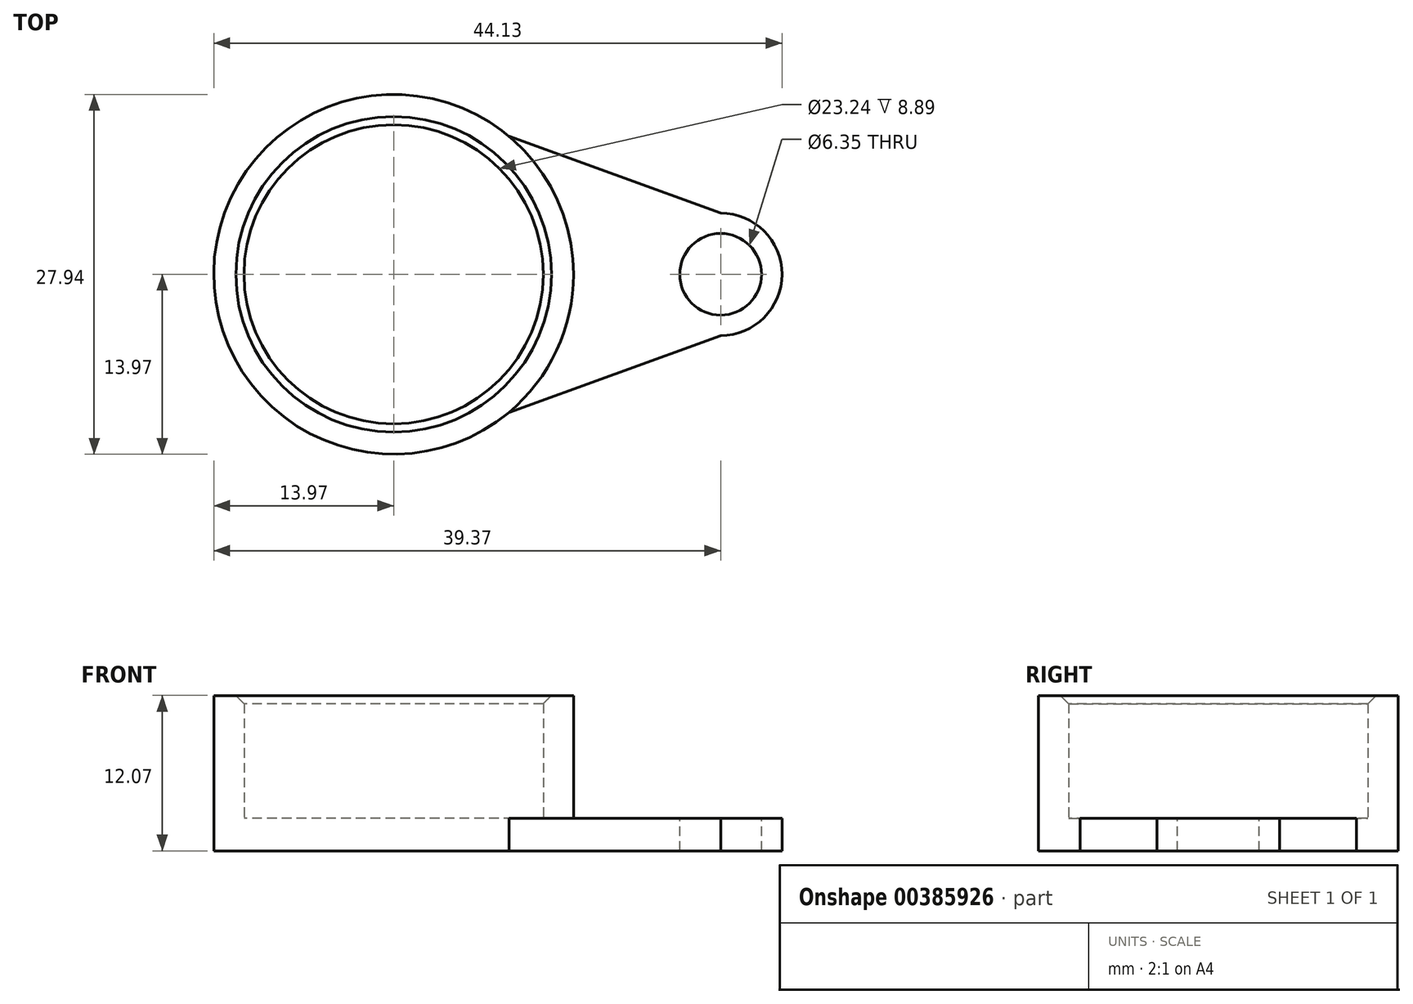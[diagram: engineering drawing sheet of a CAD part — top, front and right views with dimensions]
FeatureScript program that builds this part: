
annotation { "Feature Type Name" : "Feature", "Feature Type Description" : "" }
export const myFeature = defineFeature(function(context is Context, id is Id, definition is map)
    precondition{}
    {
        {
            var Q0;
            Q0=qCreatedBy(makeId("Top.planeOp"),FACE);
            var sketch = newSketch(context, id + "F0", { "sketchPlane" : qUnion([Q0])});
            skArc(sketch, "E0", {"start": v(8.95, 10.72) * mm, "mid": v(-13.97, 0) * mm, "end": v(8.95, -10.72) * mm});
            skArc(sketch, "E1", {"start": v(25.4, -4.76) * mm, "mid": v(30.16, 0) * mm, "end": v(25.4, 4.76) * mm});
            skLineSegment(sketch, "E2", {"start": v(8.95, -10.72) * mm, "end": v(25.4, -4.76) * mm});
            skPoint(sketch, "E3.orphan", {"position": v(25.4, 4.76) * mm});
            skPoint(sketch, "E4.start.orphan", {"position": v(0, 13.97) * mm});
            skLineSegment(sketch, "E5", {"start": v(8.95, 10.72) * mm, "end": v(25.4, 4.76) * mm});
            skPoint(sketch, "E6.orphan", {"position": v(0, -13.97) * mm});
            skSolve(sketch);
        }
        {
            var Q0;
            Q0=makeQuery(id+"F0.imprint","IMPRINT",FACE,{"disambiguationData":[TD([[makeQuery(id+"F0.imprint","IMPRINT",EDGE,{"derivedFrom":sQuery(id+"F0.wireOp",EDGE,"E0")}),1.0]])]});
            extrude(context, id + "F1", {"entities" : qUnion([Q0]), "depth" : 2.54 * mm});
        }
        {
            var Q0;
            Q0=makeQuery(id+"F1.opExtrude","CAP_FACE",FACE,{"disambiguationData":[OSD([sQuery(id+"F0.wireOp",EDGE,"E0"),sQuery(id+"F0.wireOp",EDGE,"E1"),sQuery(id+"F0.wireOp",EDGE,"E2"),sQuery(id+"F0.wireOp",EDGE,"E5")])],"isStart":false});
            var sketch = newSketch(context, id + "F2", { "sketchPlane" : qUnion([Q0])});
            skCircle(sketch, "E7", {"center": v(0, 0) * mm, "radius": 13.97 * mm});
            skCircle(sketch, "E8", {"center": v(0, 0) * mm, "radius": 11.62 * mm});
            skSolve(sketch);
        }
        {
            var Q0;
            Q0=makeQuery(id+"F2.imprint","IMPRINT",FACE,{"disambiguationData":[TD([[makeQuery(id+"F2.imprint","IMPRINT",EDGE,{"derivedFrom":sQuery(id+"F2.wireOp",EDGE,"E8")}),-1.0]])]});
            extrude(context, id + "F3", {"entities" : qUnion([Q0]), "operationType" : NewBodyOperationType.ADD, "depth" : 9.52 * mm});
        }
        {
            var Q0;
            Q0=makeQuery(id+"F3.opExtrude","CAP_EDGE",EDGE,{"disambiguationData":[OSD([sQuery(id+"F2.wireOp",EDGE,"E8")])],"isStart":false});
            chamfer(context, id + "F4", {"entities" : qUnion([Q0]), "width" : 0.64 * mm, "tangentPropagation" : true});
        }
        {
            var Q0;
            {var subQ0=sQuery(id+"F0.wireOp",EDGE,"E2");var subQ1=sQuery(id+"F0.wireOp",EDGE,"E1");var subQ2=sQuery(id+"F0.wireOp",EDGE,"E5");var subQ3=sQuery(id+"F0.wireOp",EDGE,"E0");Q0=makeQuery(id+"F3.boolean.opBoolean","SPLIT",FACE,{"disambiguationData":[TD([makeQuery(id+"F1.opExtrude","SWEPT_FACE",FACE,{"disambiguationData":[OSD([subQ3])]})])],"derivedFrom":makeQuery(id+"F1.opExtrude","CAP_FACE",FACE,{"disambiguationData":[OSD([subQ3,subQ1,subQ0,subQ2])],"isStart":false})});}
            var sketch = newSketch(context, id + "F5", { "sketchPlane" : qUnion([Q0])});
            skCircle(sketch, "E9", {"center": v(25.4, 0) * mm, "radius": 3.18 * mm});
            skSolve(sketch);
        }
        {
            var Q0;
            Q0=makeQuery(id+"F5.imprint","IMPRINT",FACE,{"disambiguationData":[TD([[makeQuery(id+"F5.imprint","IMPRINT",EDGE,{"derivedFrom":sQuery(id+"F5.wireOp",EDGE,"E9")}),1.0]])]});
            extrude(context, id + "F6", {"entities" : qUnion([Q0]), "operationType" : NewBodyOperationType.REMOVE, "endBound" : BoundingType.THROUGH_ALL, "oppositeDirection" : true, "depth" : 25.4 * mm});
        }
    });
